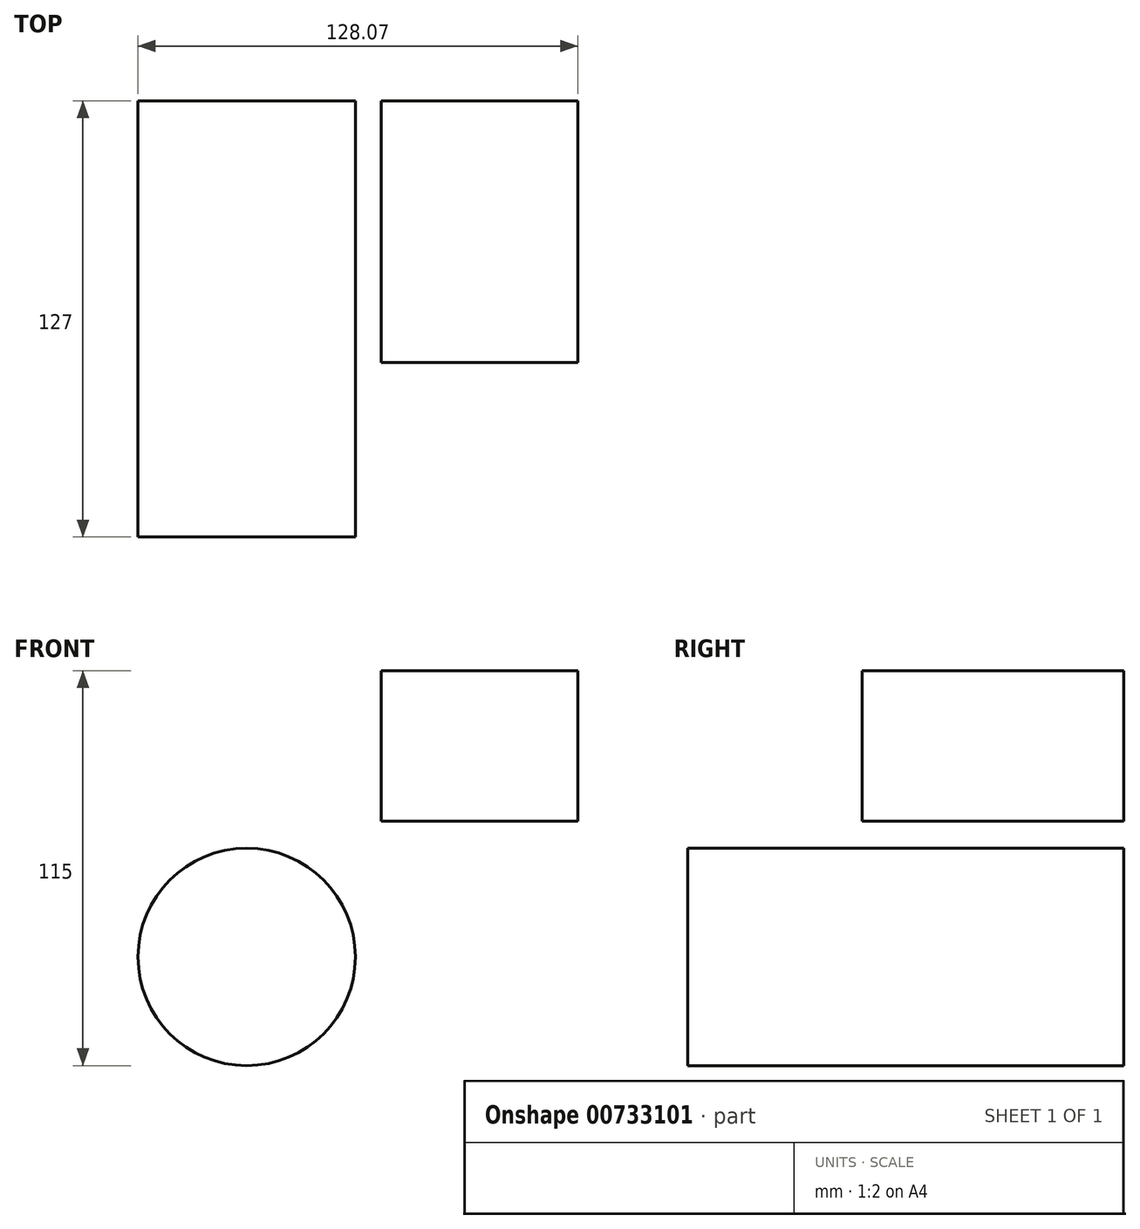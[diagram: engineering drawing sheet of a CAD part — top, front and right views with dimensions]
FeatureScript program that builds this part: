
annotation { "Feature Type Name" : "Feature", "Feature Type Description" : "" }
export const myFeature = defineFeature(function(context is Context, id is Id, definition is map)
    precondition{}
    {
        {
            var Q0;
            Q0=qCreatedBy(makeId("Front.planeOp"), FACE);
            var sketch = newSketch(context, id + "F0", { "sketchPlane" : qUnion([Q0])});
            skLineSegment(sketch, "E0.bottom", {"start": v(0, 0) * mm, "end": v(57.23, 0) * mm});
            skLineSegment(sketch, "E0.top", {"start": v(0, 43.82) * mm, "end": v(57.23, 43.82) * mm});
            skLineSegment(sketch, "E0.left", {"start": v(0, 0) * mm, "end": v(0, 43.82) * mm});
            skLineSegment(sketch, "E0.right", {"start": v(57.23, 0) * mm, "end": v(57.23, 43.82) * mm});
            skSolve(sketch);
        }
        {
            var Q0;
            Q0 = qSketchRegion(id + "F0", true);
            extrude(context, id + "F1", {"entities" : qUnion([Q0]), "depth" : 76.2 * mm, "offsetDistance" : 25.4 * mm});
        }
        {
            var Q0;
            Q0=qCreatedBy(makeId("Front.planeOp"), FACE);
            var sketch = newSketch(context, id + "F2", { "sketchPlane" : qUnion([Q0])});
            skCircle(sketch, "E1", {"center": v(-39.18, -39.53) * mm, "radius": 31.65 * mm});
            skSolve(sketch);
        }
        {
            var Q0;
            Q0 = qSketchRegion(id + "F2", true);
            extrude(context, id + "F3", {"entities" : qUnion([Q0]), "depth" : 127 * mm, "offsetDistance" : 25.4 * mm});
        }
    });
